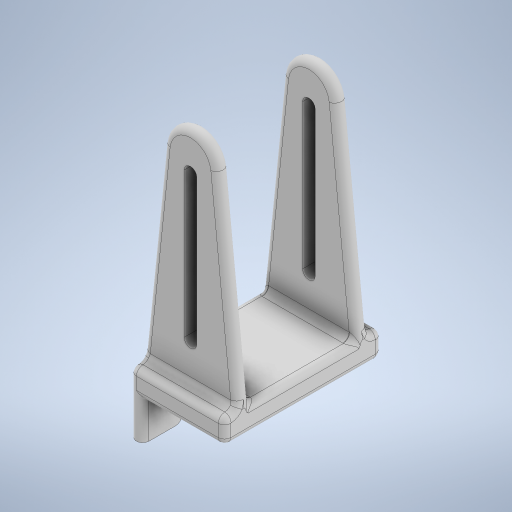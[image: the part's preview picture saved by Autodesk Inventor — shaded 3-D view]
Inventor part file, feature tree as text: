
AUTODESK INVENTOR PART (.ipt)
format: ipt  version: 2023 (Build 270158000, 158)  size: 1,192,448 bytes
history: native  units: mm
features: fillet x7, extrude x4, sketch x4, chamfer x2, other x1
ambient origin geometry x8: Origin, YZ Plane, XZ Plane, XY Plane, X Axis, Y Axis, Z Axis, Center Point
bodies: Body1 (feature_tree)
feature tree (18):
  other  "Bryła1"
  extrude  "Wyciągnięcie proste1"  Depth=50.0mm
  extrude  "Wyciągnięcie proste2"  Depth=30.0mm
  extrude  "Wyciągnięcie proste3"  Depth=8.0mm TaperAngle=0.0deg
  chamfer  "Faza1"  Distance=4.2mm
  chamfer  "Faza2"  Distance=4.2mm
  fillet  "Zaokrąglenie1"  Radius=4.0mm
  fillet  "Zaokrąglenie2"  Radius=4.0mm
  fillet  "Zaokrąglenie3"  Radius=70.0mm
  fillet  "Zaokrąglenie4"  Radius=13.0mm
  fillet  "Zaokrąglenie5"  Radius=13.0mm
  extrude  "Wyciągnięcie proste4"  Depth=10.0mm
  fillet  "Zaokrąglenie6"  Radius=10.0mm
  fillet  "Zaokrąglenie7"  Radius=70.0mm
  sketch  "Szkic1"
  sketch  "Szkic2"
  sketch  "Szkic3"
  sketch  "Szkic4"
